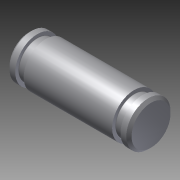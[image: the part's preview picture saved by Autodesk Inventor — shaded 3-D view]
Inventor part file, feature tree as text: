
AUTODESK INVENTOR PART (.ipt)
format: ipt  version: 2012 (Build 160160000, 160)  size: 140,800 bytes
history: native  units: in
note: dims shown in document units (in); Inventor stores cm internally (conversion verified against a paired STEP export)
features: other x49, revolve x1, sketch x1
ambient origin geometry x8: Origin, YZ Plane, XZ Plane, XY Plane, X Axis, Y Axis, Z Axis, Center Point
bodies: Solid1 (feature_tree)
feature tree (51):
  revolve  "Revolution1"  [1 undecoded]
  other  "pin_XY"
  other  "pin_YZ"
  other  "pin_ZX"
  other  "pin_X"
  other  "pin_Y"
  other  "pin_Z"
  other  "pin_Center"
  other  "rr1_XY"
  other  "rr1_YZ"
  other  "rr1_ZX"
  other  "rr1_X"
  other  "rr1_Y"
  other  "rr1_Z"
  other  "rr1_Center"
  other  "rr2_XY"
  other  "rr2_YZ"
  other  "rr2_ZX"
  other  "rr2_X"
  other  "rr2_Y"
  other  "rr2_Z"
  other  "rr2_Center"
  other  "w21_XY"
  other  "w21_YZ"
  other  "w21_ZX"
  other  "w21_X"
  other  "w21_Y"
  other  "w21_Z"
  other  "w21_Center"
  other  "w22_XY"
  other  "w22_YZ"
  other  "w22_ZX"
  other  "w22_X"
  other  "w22_Y"
  other  "w22_Z"
  other  "w22_Center"
  other  "p1_XY"
  other  "p1_YZ"
  other  "p1_ZX"
  other  "p1_X"
  other  "p1_Y"
  other  "p1_Z"
  other  "p1_Center"
  other  "p2_XY"
  other  "p2_YZ"
  other  "p2_ZX"
  other  "p2_X"
  other  "p2_Y"
  other  "p2_Z"
  other  "p2_Center"
  sketch  "Sketch_1"  dims[d0=360.0deg]
note: 1 required parameter value undecoded (feature->parameter linkage not recoverable at this tier; creation-order binding heuristic only, values carry confidence <= 0.55)
